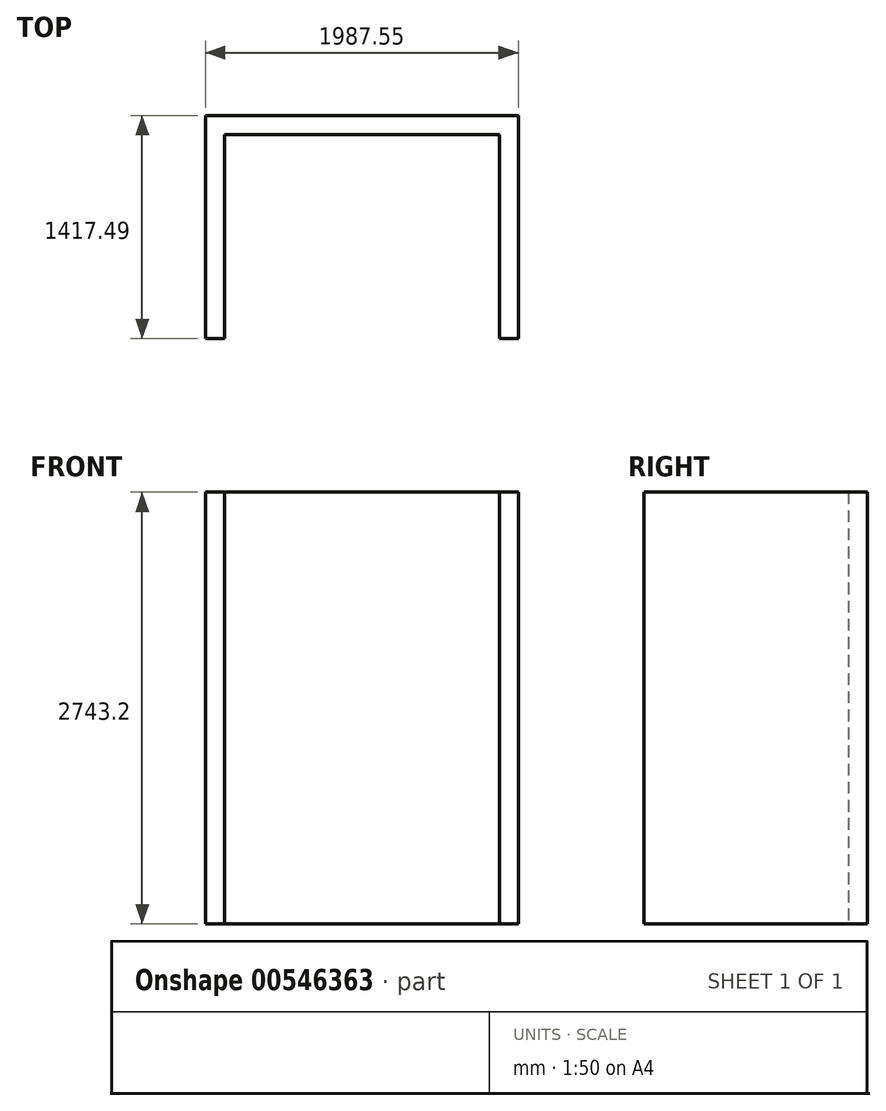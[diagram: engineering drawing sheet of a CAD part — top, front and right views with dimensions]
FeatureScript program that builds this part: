
annotation { "Feature Type Name" : "Feature", "Feature Type Description" : "" }
export const myFeature = defineFeature(function(context is Context, id is Id, definition is map)
    precondition{}
    {
        {
            var Q0;
            Q0=qCreatedBy(makeId("Top.planeOp"),FACE);
            var sketch = newSketch(context, id + "F0", { "sketchPlane" : qUnion([Q0])});
            skLineSegment(sketch, "E0", {"start": v(-1031.2, -699.91) * mm, "end": v(-1031.2, 717.58) * mm});
            skLineSegment(sketch, "E1", {"start": v(-1031.2, 717.58) * mm, "end": v(956.35, 717.58) * mm});
            skLineSegment(sketch, "E2", {"start": v(956.35, 717.58) * mm, "end": v(956.35, -699.91) * mm});
            skLineSegment(sketch, "E3", {"start": v(956.35, -699.91) * mm, "end": v(835.7, -699.91) * mm});
            skLineSegment(sketch, "E4", {"start": v(835.7, -699.91) * mm, "end": v(835.7, 596.93) * mm});
            skLineSegment(sketch, "E5", {"start": v(835.7, 596.93) * mm, "end": v(-910.55, 596.93) * mm});
            skLineSegment(sketch, "E6", {"start": v(-910.55, 596.93) * mm, "end": v(-910.55, -699.91) * mm});
            skLineSegment(sketch, "E7", {"start": v(-910.55, -699.91) * mm, "end": v(-1031.2, -699.91) * mm});
            skSolve(sketch);
        }
        {
            var Q0;
            Q0=makeQuery(id+"F0.imprint","IMPRINT",FACE,{"disambiguationData":[TD([[makeQuery(id+"F0.imprint","IMPRINT",EDGE,{"derivedFrom":sQuery(id+"F0.wireOp",EDGE,"E0")}),-1.0]])]});
            extrude(context, id + "F1", {"entities" : qUnion([Q0]), "depth" : 2743.2 * mm, "offsetDistance" : 25.4 * mm});
        }
    });
